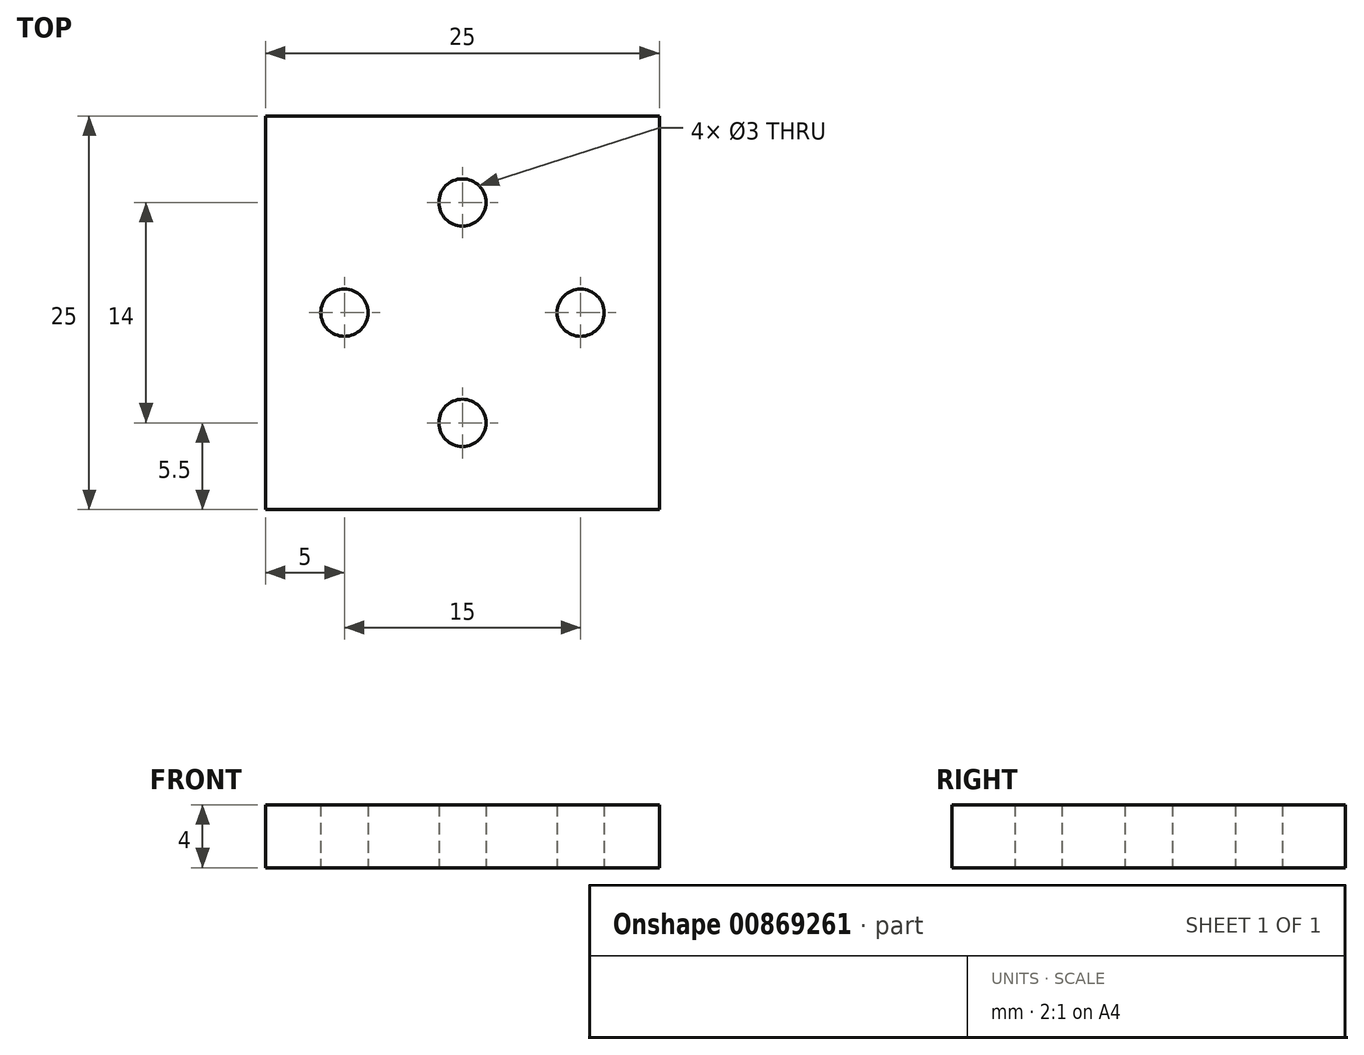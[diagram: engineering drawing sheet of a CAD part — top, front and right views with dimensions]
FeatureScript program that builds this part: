
annotation { "Feature Type Name" : "Feature", "Feature Type Description" : "" }
export const myFeature = defineFeature(function(context is Context, id is Id, definition is map)
    precondition{}
    {
        {
            var Q0;
            Q0=qCreatedBy(makeId("Top.planeOp"),FACE);
            var sketch = newSketch(context, id + "F0", { "sketchPlane" : qUnion([Q0])});
            skLineSegment(sketch, "E0.bottom", {"start": v(12.5, -12.5) * mm, "end": v(-12.5, -12.5) * mm});
            skLineSegment(sketch, "E0.top", {"start": v(12.5, 12.5) * mm, "end": v(-12.5, 12.5) * mm});
            skLineSegment(sketch, "E0.left", {"start": v(12.5, -12.5) * mm, "end": v(12.5, 12.5) * mm});
            skLineSegment(sketch, "E0.right", {"start": v(-12.5, -12.5) * mm, "end": v(-12.5, 12.5) * mm});
            skPoint(sketch, "E0.middle", {"position": v(0, 0) * mm});
            skLineSegment(sketch, "E1.bottom", {"start": v(7.5, 0) * mm, "end": v(-7.5, 0) * mm, "construction": true});
            skLineSegment(sketch, "E1.top", {"start": v(7.5, 0) * mm, "end": v(-7.5, 0) * mm, "construction": true});
            skLineSegment(sketch, "E1.left", {"start": v(7.5, 0) * mm, "end": v(7.5, 0) * mm});
            skLineSegment(sketch, "E1.right", {"start": v(-7.5, 0) * mm, "end": v(-7.5, 0) * mm});
            skLineSegment(sketch, "E2.bottom", {"start": v(0, -7) * mm, "end": v(0, -7) * mm});
            skLineSegment(sketch, "E2.top", {"start": v(0, 7) * mm, "end": v(0, 7) * mm});
            skLineSegment(sketch, "E2.left", {"start": v(0, -7) * mm, "end": v(0, 7) * mm, "construction": true});
            skLineSegment(sketch, "E2.right", {"start": v(0, -7) * mm, "end": v(0, 7) * mm, "construction": true});
            skSolve(sketch);
        }
        {
            var Q0;
            Q0=makeQuery(id+"F0.imprint","IMPRINT",FACE,{"disambiguationData":[TD([[makeQuery(id+"F0.imprint","IMPRINT",EDGE,{"derivedFrom":sQuery(id+"F0.wireOp",EDGE,"E0.bottom")}),-1.0]])]});
            var Q1;
            Q1=makeQuery(id+"F0.imprint","IMPRINT",FACE,{"disambiguationData":[TD([[makeQuery(id+"F0.imprint","IMPRINT",EDGE,{"derivedFrom":sQuery(id+"F0.wireOp",EDGE,"E1.bottom")}),-1.0]])]});
            var Q2;
            {var subQ0=sQuery(id+"F0.wireOp",EDGE,"E1.top");Q2=makeQuery(id+"F0.imprint","IMPRINT",FACE,{"disambiguationData":[TD([[makeQuery(id+"F0.imprint","IMPRINT",EDGE,{"derivedFrom":subQ0}),1.0]])]});}
            var Q3;
            Q3=makeQuery(id+"F0.imprint","IMPRINT",FACE,{"disambiguationData":[TD([[makeQuery(id+"F0.imprint","IMPRINT",EDGE,{"derivedFrom":sQuery(id+"F0.wireOp",EDGE,"ycsBIgkZ-ymJQ-sAMf-OLlC-tRUSnlsIV0g0.bottom")}),-1.0]])]});
            extrude(context, id + "F1", {"entities" : qUnion([Q0, Q1, Q2, Q3]), "depth" : 4 * mm, "offsetDistance" : 25 * mm});
        }
        {
            var Q0;
            Q0=sQuery(id+"F0.wireOp",VERTEX,"E1.top.end");
            var Q1;
            Q1=sQuery(id+"F0.wireOp",VERTEX,"E1.bottom.start");
            var Q2;
            Q2=sQuery(id+"F0.wireOp",VERTEX,"E2.left.end");
            var Q3;
            Q3=sQuery(id+"F0.wireOp",VERTEX,"E2.left.start");
            var Q4;
            Q4=makeQuery(id+"F1.opExtrude","SWEPT_BODY",BODY,{"disambiguationData":[OSD([sQuery(id+"F0.wireOp",EDGE,"E0.bottom"),sQuery(id+"F0.wireOp",EDGE,"E0.top"),sQuery(id+"F0.wireOp",EDGE,"E0.left"),sQuery(id+"F0.wireOp",EDGE,"E0.right")])]});
            hole(context, id + "F2", {"style" : HoleStyle.SIMPLE, "endStyle" : HoleEndStyle.THROUGH, "oppositeDirection" : true, "holeDiameter" : 3 * mm, "majorDiameter" : 5 * mm, "isTappedThrough" : true, "tappedDepth" : 12 * mm, "tapClearance" : 3, "locations" : qUnion([Q0, Q1, Q2, Q3]), "scope" : qUnion([Q4])});
        }
    });
